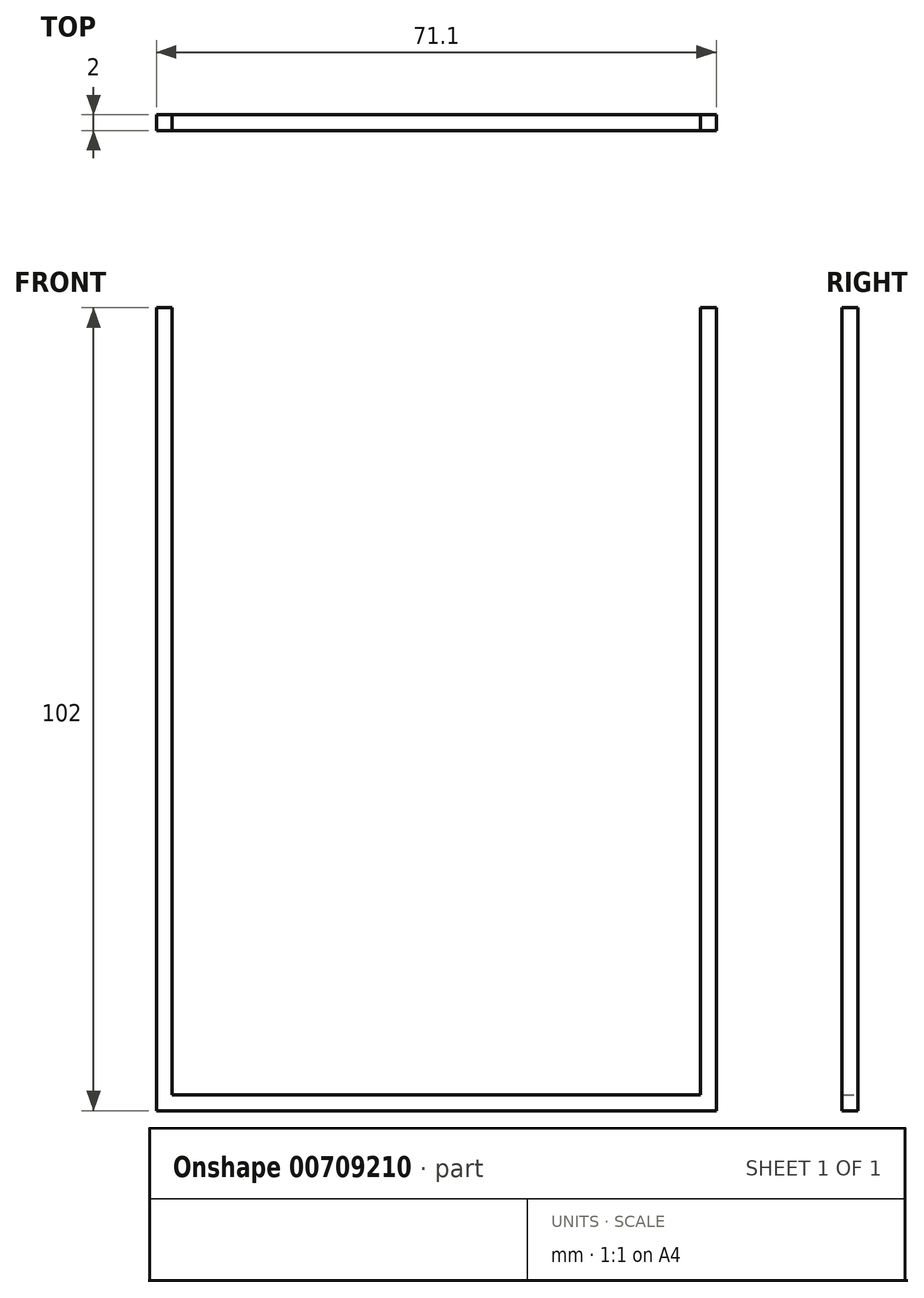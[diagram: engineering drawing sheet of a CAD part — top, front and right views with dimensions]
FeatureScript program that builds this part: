
annotation { "Feature Type Name" : "Feature", "Feature Type Description" : "" }
export const myFeature = defineFeature(function(context is Context, id is Id, definition is map)
    precondition{}
    {
        {
            var Q0;
            Q0=qCreatedBy(makeId("Front.planeOp"),FACE);
            var sketch = newSketch(context, id + "F0", { "sketchPlane" : qUnion([Q0])});
            skLineSegment(sketch, "E0.bottom", {"start": v(33.55, 50) * mm, "end": v(-33.55, 50) * mm});
            skLineSegment(sketch, "E0.top", {"start": v(33.55, -50) * mm, "end": v(-33.55, -50) * mm});
            skLineSegment(sketch, "E0.left", {"start": v(33.55, 50) * mm, "end": v(33.55, -50) * mm});
            skLineSegment(sketch, "E0.right", {"start": v(-33.55, 50) * mm, "end": v(-33.55, -50) * mm});
            skPoint(sketch, "E0.middle", {"position": v(0, 0) * mm});
            skLineSegment(sketch, "E1.bottom", {"start": v(35.55, 50) * mm, "end": v(-35.55, 50) * mm});
            skLineSegment(sketch, "E1.top", {"start": v(35.55, -52) * mm, "end": v(-35.55, -52) * mm});
            skLineSegment(sketch, "E1.left", {"start": v(35.55, 50) * mm, "end": v(35.55, -52) * mm});
            skLineSegment(sketch, "E1.right", {"start": v(-35.55, 50) * mm, "end": v(-35.55, -52) * mm});
            skPoint(sketch, "E1.middle", {"position": v(0, -1) * mm});
            skSolve(sketch);
        }
        {
            var Q0;
            Q0=makeQuery(id+"F0.imprint","IMPRINT",FACE,{"disambiguationData":[TD([[makeQuery(id+"F0.imprint","IMPRINT",EDGE,{"derivedFrom":sQuery(id+"F0.wireOp",EDGE,"E0.top")}),1.0]])]});
            extrude(context, id + "F1", {"entities" : qUnion([Q0]), "depth" : 2 * mm, "offsetDistance" : 25 * mm});
        }
    });
